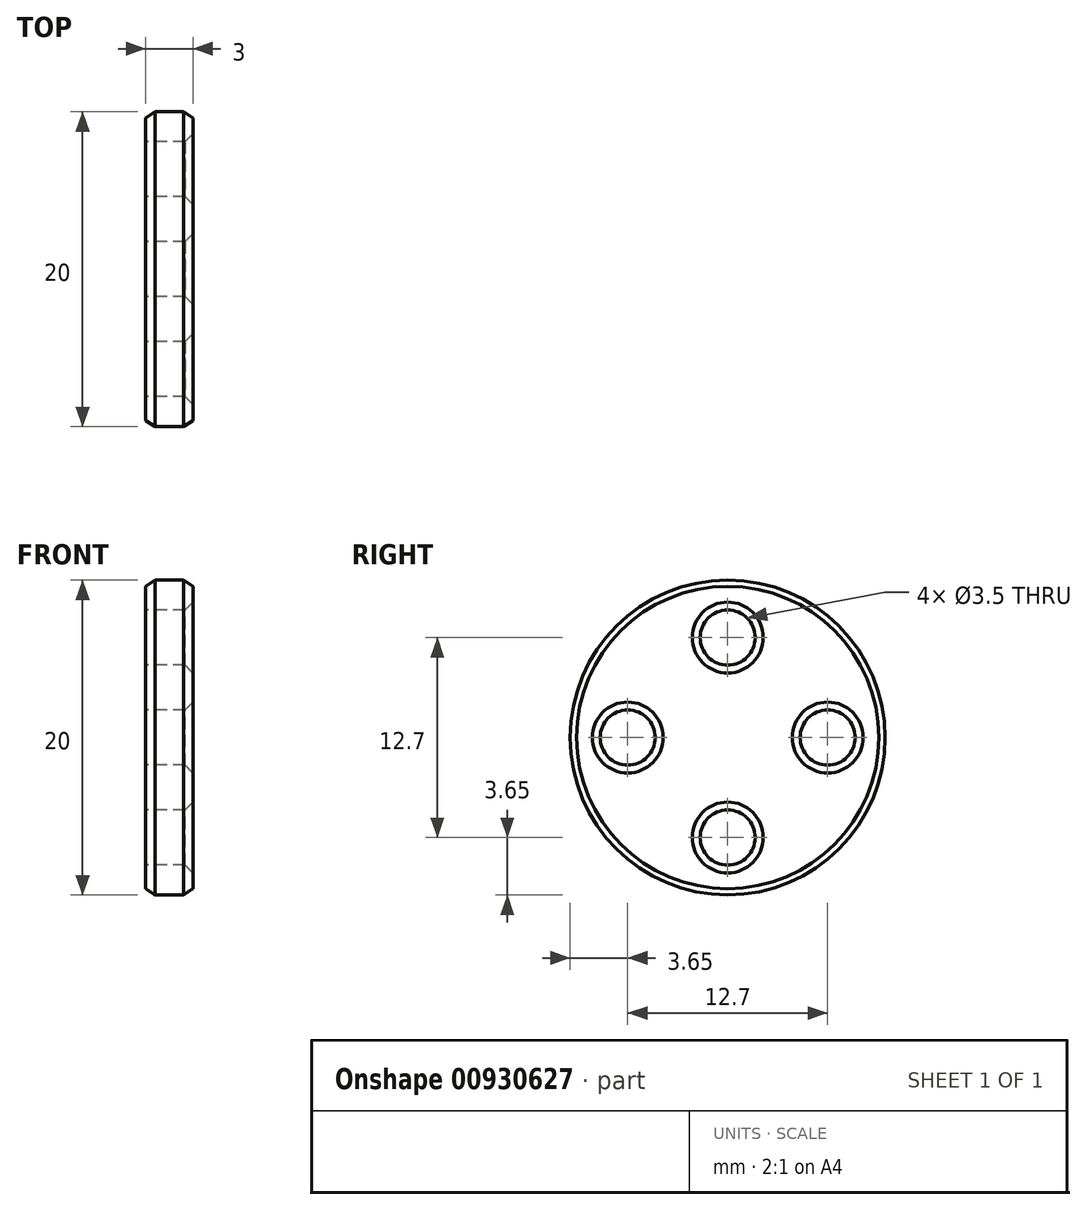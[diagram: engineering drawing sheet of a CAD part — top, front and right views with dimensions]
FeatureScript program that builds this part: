
annotation { "Feature Type Name" : "Feature", "Feature Type Description" : "" }
export const myFeature = defineFeature(function(context is Context, id is Id, definition is map)
    precondition{}
    {
        {
            var Q0;
            Q0=qCreatedBy(makeId("Right.planeOp"),FACE);
            var sketch = newSketch(context, id + "F0", { "sketchPlane" : qUnion([Q0])});
            skCircle(sketch, "E0", {"center": v(0, 0) * mm, "radius": 10 * mm});
            skCircle(sketch, "E1", {"center": v(0, 6.35) * mm, "radius": 1.75 * mm});
            skCircle(sketch, "E2", {"center": v(-6.35, 0) * mm, "radius": 1.75 * mm});
            skCircle(sketch, "E3", {"center": v(6.35, 0) * mm, "radius": 1.75 * mm});
            skCircle(sketch, "E4", {"center": v(0, -6.35) * mm, "radius": 1.75 * mm});
            skSolve(sketch);
        }
        {
            var Q0;
            Q0=qSketchRegion(id+"F0",true);
            extrude(context, id + "F1", {"entities" : qUnion([Q0]), "depth" : 3 * mm, "offsetDistance" : 25 * mm});
        }
        {
            var Q0;
            Q0=makeQuery(id+"F1.opExtrude","CAP_EDGE",EDGE,{"disambiguationData":[OSD([sQuery(id+"F0.wireOp",EDGE,"E2")])],"isStart":false});
            var Q1;
            Q1=makeQuery(id+"F1.opExtrude","CAP_EDGE",EDGE,{"disambiguationData":[OSD([sQuery(id+"F0.wireOp",EDGE,"E1")])],"isStart":false});
            var Q2;
            Q2=makeQuery(id+"F1.opExtrude","CAP_EDGE",EDGE,{"disambiguationData":[OSD([sQuery(id+"F0.wireOp",EDGE,"E3")])],"isStart":false});
            var Q3;
            Q3=makeQuery(id+"F1.opExtrude","CAP_EDGE",EDGE,{"disambiguationData":[OSD([sQuery(id+"F0.wireOp",EDGE,"E4")])],"isStart":false});
            chamfer(context, id + "F2", {"entities" : qUnion([Q0, Q1, Q2, Q3]), "width" : 0.5 * mm, "tangentPropagation" : true});
        }
        {
            var Q0;
            Q0=makeQuery(id+"F1.opExtrude","CAP_EDGE",EDGE,{"disambiguationData":[OSD([sQuery(id+"F0.wireOp",EDGE,"E0")])],"isStart":false});
            var Q1;
            Q1=makeQuery(id+"F1.opExtrude","CAP_EDGE",EDGE,{"disambiguationData":[OSD([sQuery(id+"F0.wireOp",EDGE,"E0")])],"isStart":true});
            chamfer(context, id + "F3", {"entities" : qUnion([Q0, Q1]), "chamferType" : ChamferType.TWO_OFFSETS, "width1" : 0.4 * mm, "oppositeDirection" : false, "width2" : 0.6 * mm, "tangentPropagation" : true});
        }
    });
